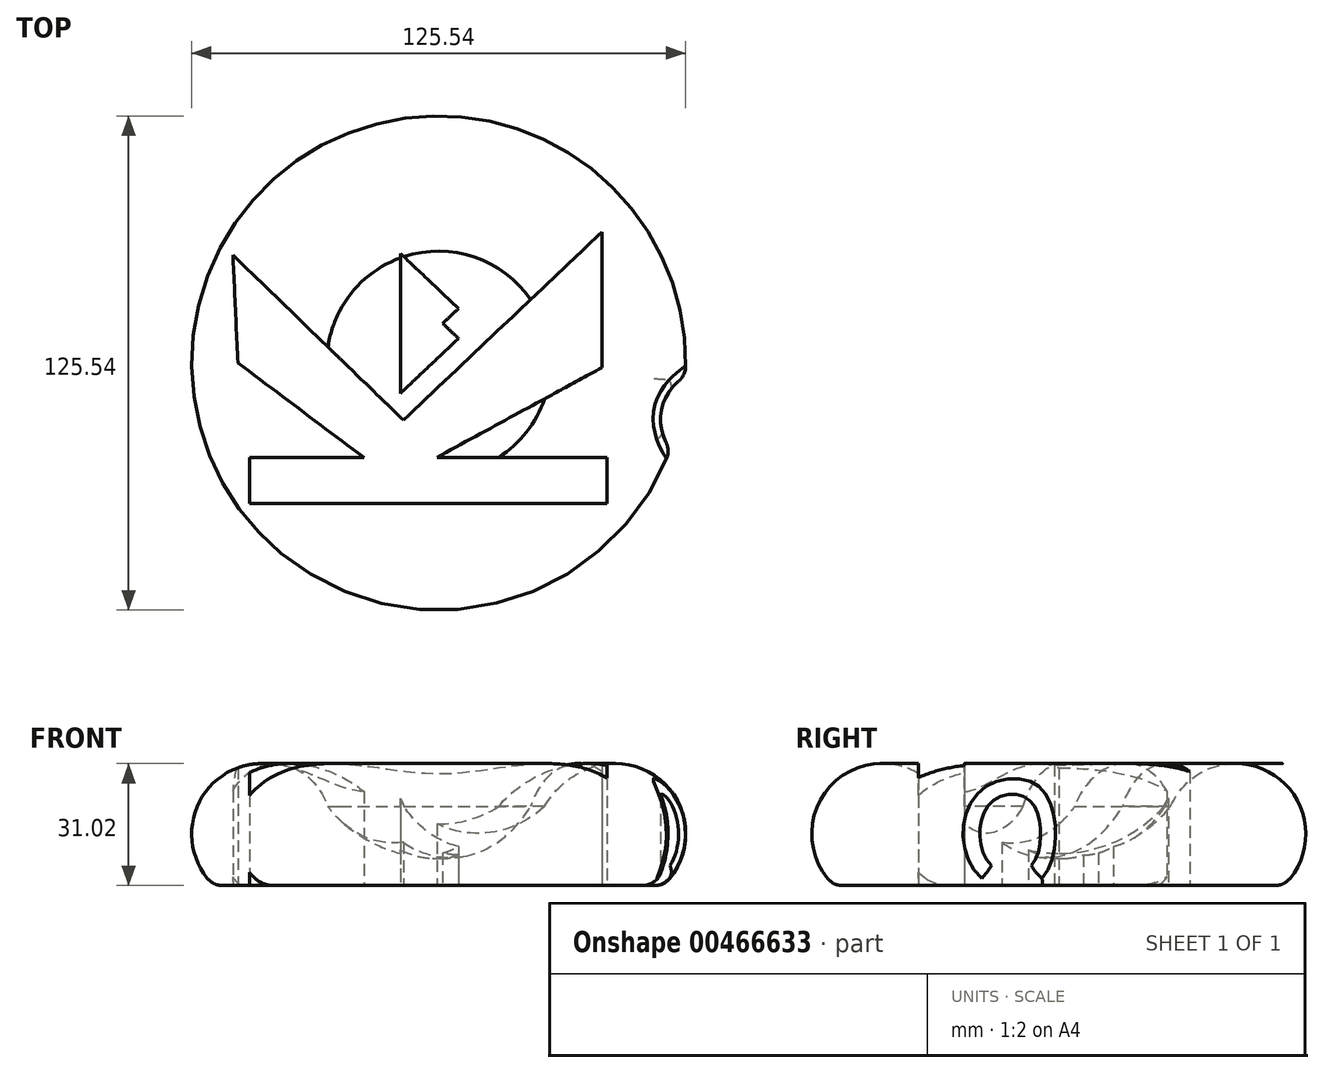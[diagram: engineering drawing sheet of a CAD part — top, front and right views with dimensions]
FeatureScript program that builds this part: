
annotation { "Feature Type Name" : "Feature", "Feature Type Description" : "" }
export const myFeature = defineFeature(function(context is Context, id is Id, definition is map)
    precondition{}
    {
        {
            var Q0;
            Q0=qCreatedBy(makeId("Front.planeOp"),FACE);
            var sketch = newSketch(context, id + "F0", { "sketchPlane" : qUnion([Q0])});
            skArc(sketch, "E0", {"start": v(-37.8, 10.08) * mm, "mid": v(-49.93, 41.1) * mm, "end": v(-62.05, 10.08) * mm});
            skLineSegment(sketch, "E1.bottom", {"start": v(-37.8, 10.08) * mm, "end": v(-5.04, 10.08) * mm});
            skLineSegment(sketch, "E1.right", {"start": v(-5.04, 10.08) * mm, "end": v(-5.04, 16.96) * mm});
            skPoint(sketch, "E2.visualSharp", {"position": v(-5.04, 10.08) * mm});
            skLineSegment(sketch, "E3", {"start": v(-62.05, 10.08) * mm, "end": v(-37.8, 10.08) * mm});
            skLineSegment(sketch, "E4.left", {"start": v(-37.8, 10.08) * mm, "end": v(-33.44, 30.14) * mm});
            skLineSegment(sketch, "E4.right", {"start": v(-5.04, 10.08) * mm, "end": v(-5.04, 10.08) * mm});
            skArc(sketch, "E5", {"start": v(-33.44, 30.14) * mm, "mid": v(-20.7, 20.41) * mm, "end": v(-5.04, 16.96) * mm});
            skSolve(sketch);
        }
        {
            var Q0;
            Q0 = qSketchRegion(id + "F0", true);
            var Q1;
            {var subQ0=sQuery(id+"F0.wireOp",EDGE,"E4.left");Q1=makeQuery(id+"F0.imprint","IMPRINT",FACE,{"disambiguationData":[TD([[makeQuery(id+"F0.imprint","IMPRINT",EDGE,{"derivedFrom":subQ0}),-1.0]])]});}
            var Q2;
            {var subQ0=sQuery(id+"F0.wireOp",EDGE,"E3");Q2=makeQuery(id+"F0.imprint","IMPRINT",FACE,{"disambiguationData":[TD([[makeQuery(id+"F0.imprint","IMPRINT",EDGE,{"derivedFrom":subQ0}),1.0]])]});}
            var Q3;
            Q3=makeQuery(id+"F0.imprint","IMPRINT",FACE,{"disambiguationData":[TD([[makeQuery(id+"F0.imprint","IMPRINT",EDGE,{"derivedFrom":sQuery(id+"F0.wireOp",EDGE,"E1.right")}),1.0]])]});
            var Q4;
            Q4=sQuery(id+"F0.wireOp",EDGE,"E1.right");
            revolve(context, id + "F1", {"entities" : qUnion([Q0, Q1, Q2, Q3]), "axis" : qUnion([Q4]), "revolveType" : RevolveType.FULL});
        }
        {
            var Q0;
            Q0=qCreatedBy(makeId("Top.planeOp"),FACE);
            var sketch = newSketch(context, id + "F2", { "sketchPlane" : qUnion([Q0])});
            skCircle(sketch, "E6", {"center": v(64.05, -14.38) * mm, "radius": 12.7 * mm});
            skSolve(sketch);
        }
        {
            var Q0;
            Q0=makeQuery(id+"F2.imprint","IMPRINT",FACE,{"disambiguationData":[TD([[makeQuery(id+"F2.imprint","IMPRINT",EDGE,{"derivedFrom":sQuery(id+"F2.wireOp",EDGE,"E6")}),1.0]])]});
            extrude(context, id + "F3", {"entities" : qUnion([Q0]), "operationType" : NewBodyOperationType.REMOVE, "endBound" : BoundingType.THROUGH_ALL, "depth" : 25.4 * mm});
        }
        {
            var Q0;
            Q0=makeQuery(id+"F3.boolean.opBoolean","INTERSECT",EDGE,{"derivedFrom":[makeQuery(id+"F1.opRevolve","SWEPT_FACE",FACE,{"disambiguationData":[OSD([sQuery(id+"F0.wireOp",EDGE,"E0")])]}),makeQuery(id+"F3.opExtrude","SWEPT_FACE",FACE,{"disambiguationData":[OSD([sQuery(id+"F2.wireOp",EDGE,"E6")])]})]});
            fillet(context, id + "F4", {"entities" : qUnion([Q0]), "radius" : 5.08 * mm, "tangentPropagation" : true, "allowEdgeOverflow" : false});
        }
        {
            var Q0;
            Q0=makeQuery(id+"F1.opRevolve","SWEPT_EDGE",EDGE,{"disambiguationData":[OSD([sQuery(id+"F0.wireOp",EDGE,"E0"),sQuery(id+"F0.wireOp",EDGE,"E3")])]});
            fillet(context, id + "F5", {"entities" : qUnion([Q0]), "radius" : 5.08 * mm, "tangentPropagation" : true, "allowEdgeOverflow" : false});
        }
        {
            var Q0;
            Q0=qCreatedBy(makeId("Top.planeOp"),FACE);
            var sketch = newSketch(context, id + "F6", { "sketchPlane" : qUnion([Q0])});
            skLineSegment(sketch, "E7.bottom", {"start": v(-53.06, -35.7) * mm, "end": v(37.75, -35.7) * mm});
            skLineSegment(sketch, "E7.top", {"start": v(-53.06, -23.99) * mm, "end": v(-24.03, -23.99) * mm});
            skLineSegment(sketch, "E7.left", {"start": v(-53.06, -35.7) * mm, "end": v(-53.06, -23.99) * mm});
            skLineSegment(sketch, "E7.right", {"start": v(37.75, -35.7) * mm, "end": v(37.75, -23.99) * mm});
            skLineSegment(sketch, "E8", {"start": v(-5.5, -23.99) * mm, "end": v(36.46, -1.16) * mm});
            skLineSegment(sketch, "E9", {"start": v(36.46, -1.16) * mm, "end": v(36.46, 33.28) * mm});
            skLineSegment(sketch, "E10", {"start": v(36.46, 33.28) * mm, "end": v(-14.01, -14.5) * mm});
            skLineSegment(sketch, "E11", {"start": v(-24.03, -23.99) * mm, "end": v(-56.05, 0) * mm});
            skLineSegment(sketch, "E12", {"start": v(-56.05, 0) * mm, "end": v(-57.3, 27.43) * mm});
            skLineSegment(sketch, "E13", {"start": v(-57.3, 27.43) * mm, "end": v(-14.01, -14.5) * mm});
            skLineSegment(sketch, "E14.trimOffspring", {"start": v(-5.5, -23.99) * mm, "end": v(37.75, -23.99) * mm});
            skLineSegment(sketch, "E15", {"start": v(-14.76, -7.74) * mm, "end": v(-14.76, 27.82) * mm});
            skLineSegment(sketch, "E16", {"start": v(-14.76, 27.82) * mm, "end": v(0, 13.85) * mm});
            skLineSegment(sketch, "E17", {"start": v(0, 13.85) * mm, "end": v(-4.02, 10.04) * mm});
            skLineSegment(sketch, "E18", {"start": v(-4.02, 10.04) * mm, "end": v(0, 6.23) * mm});
            skLineSegment(sketch, "E19", {"start": v(0, 6.23) * mm, "end": v(-14.76, -7.74) * mm});
            skPoint(sketch, "E20", {"position": v(-14.76, 10.04) * mm});
            skSolve(sketch);
        }
        {
            var Q0;
            Q0 = qSketchRegion(id + "F6", true);
            extrude(context, id + "F7", {"entities" : qUnion([Q0]), "operationType" : NewBodyOperationType.REMOVE, "endBound" : BoundingType.THROUGH_ALL, "depth" : 25.4 * mm});
        }
    });
